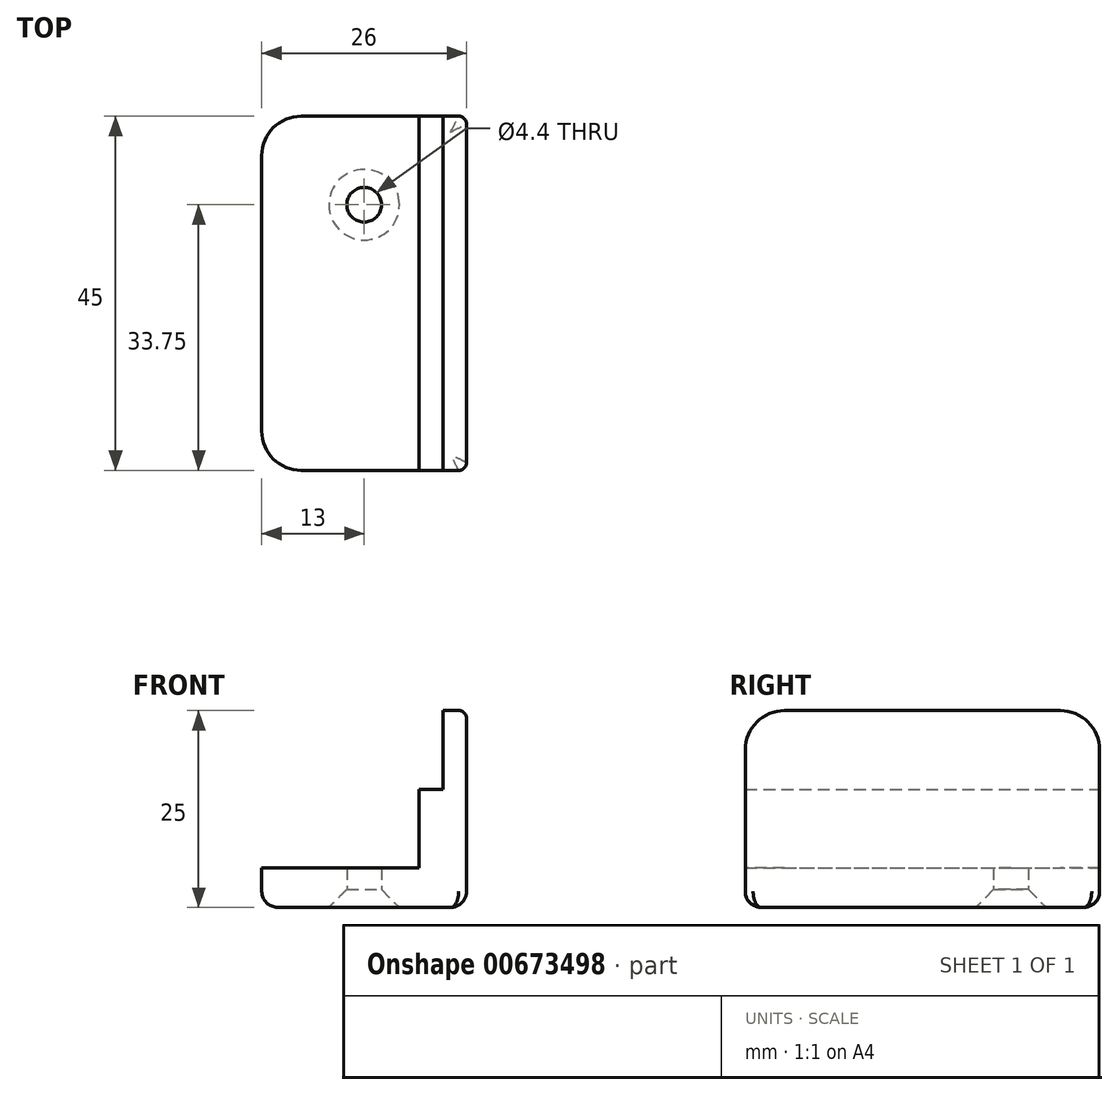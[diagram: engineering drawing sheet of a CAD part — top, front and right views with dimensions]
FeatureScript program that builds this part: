
annotation { "Feature Type Name" : "Feature", "Feature Type Description" : "" }
export const myFeature = defineFeature(function(context is Context, id is Id, definition is map)
    precondition{}
    {
        {
            var Q0;
            Q0=qCreatedBy(makeId("Front.planeOp"),FACE);
            var sketch = newSketch(context, id + "F0", { "sketchPlane" : qUnion([Q0])});
            skLineSegment(sketch, "E0", {"start": v(0, 25) * mm, "end": v(0, 0) * mm});
            skLineSegment(sketch, "E1", {"start": v(0, 0) * mm, "end": v(-26, 0) * mm});
            skLineSegment(sketch, "E2", {"start": v(-26, 0) * mm, "end": v(-26, 5) * mm});
            skLineSegment(sketch, "E3", {"start": v(-26, 5) * mm, "end": v(-6, 5) * mm});
            skLineSegment(sketch, "E4", {"start": v(-6, 5) * mm, "end": v(-6, 15) * mm});
            skLineSegment(sketch, "E5", {"start": v(-6, 15) * mm, "end": v(-3, 15) * mm});
            skLineSegment(sketch, "E6", {"start": v(-3, 15) * mm, "end": v(-3, 25) * mm});
            skLineSegment(sketch, "E7", {"start": v(-3, 25) * mm, "end": v(0, 25) * mm});
            skSolve(sketch);
        }
        {
            var Q0;
            Q0=qSketchRegion(id+"F0",true);
            extrude(context, id + "F1", {"entities" : qUnion([Q0]), "endBound" : BoundingType.SYMMETRIC, "depth" : 45 * mm, "offsetDistance" : 25 * mm});
        }
        {
            var Q0;
            Q0=makeQuery(id+"F1.opExtrude","SWEPT_FACE",FACE,{"disambiguationData":[OSD([sQuery(id+"F0.wireOp",EDGE,"E1")])]});
            var sketch = newSketch(context, id + "F2", { "sketchPlane" : qUnion([Q0])});
            skLineSegment(sketch, "E8", {"start": v(-26, 0) * mm, "end": v(0, 0) * mm, "construction": true});
            skPoint(sketch, "E9", {"position": v(-13, -11.25) * mm});
            skSolve(sketch);
        }
        {
            var Q0;
            Q0=sQuery(id+"F2.wireOp",VERTEX,"E9");
            var Q1;
            Q1=makeQuery(id+"F1.opExtrude","SWEPT_BODY",BODY,{"disambiguationData":[OSD([sQuery(id+"F0.wireOp",EDGE,"E0"),sQuery(id+"F0.wireOp",EDGE,"E1"),sQuery(id+"F0.wireOp",EDGE,"E2"),sQuery(id+"F0.wireOp",EDGE,"E3"),sQuery(id+"F0.wireOp",EDGE,"E4"),sQuery(id+"F0.wireOp",EDGE,"E5"),sQuery(id+"F0.wireOp",EDGE,"E6"),sQuery(id+"F0.wireOp",EDGE,"E7")])]});
            hole(context, id + "F3", {"style" : HoleStyle.C_SINK, "endStyle" : HoleEndStyle.THROUGH, "standardTappedOrClearance" : lookupTablePath({ "standard" : "ISO", "fit" : "Normal", "size" : "M4", "type" : "Clearance" }), "standardBlindInLast" : lookupTablePath({ "fit" : "Standard", "standard" : "ISO", "size" : "M4", "type" : "Clearance" }), "holeDiameter" : 4.4 * mm, "cSinkDiameter" : 8.96 * mm, "cSinkAngle" : 90 * degree, "majorDiameter" : 5 * mm, "isTappedThrough" : true, "tappedDepth" : 12 * mm, "tapClearance" : 3, "locations" : qUnion([Q0]), "scope" : qUnion([Q1])});
        }
        {
            var Q0;
            Q0=makeQuery(id+"F1.opExtrude","CAP_EDGE",EDGE,{"disambiguationData":[OSD([sQuery(id+"F0.wireOp",EDGE,"E2")])],"isStart":true});
            var Q1;
            Q1=makeQuery(id+"F1.opExtrude","CAP_EDGE",EDGE,{"disambiguationData":[OSD([sQuery(id+"F0.wireOp",EDGE,"E2")])],"isStart":false});
            var Q2;
            Q2=makeQuery(id+"F1.opExtrude","CAP_EDGE",EDGE,{"disambiguationData":[OSD([sQuery(id+"F0.wireOp",EDGE,"E7")])],"isStart":false});
            var Q3;
            Q3=makeQuery(id+"F1.opExtrude","CAP_EDGE",EDGE,{"disambiguationData":[OSD([sQuery(id+"F0.wireOp",EDGE,"E7")])],"isStart":true});
            fillet(context, id + "F4", {"entities" : qUnion([Q0, Q1, Q2, Q3]), "radius" : 5 * mm, "tangentPropagation" : true, "allowEdgeOverflow" : false});
        }
        {
            var Q0;
            Q0=makeQuery(id+"F1.opExtrude","CAP_EDGE",EDGE,{"disambiguationData":[OSD([sQuery(id+"F0.wireOp",EDGE,"E0")])],"isStart":true});
            fillet(context, id + "F5", {"entities" : qUnion([Q0]), "radius" : 1 * mm, "tangentPropagation" : true, "allowEdgeOverflow" : false});
        }
        {
            var Q0;
            Q0=makeQuery(id+"F1.opExtrude","SWEPT_EDGE",EDGE,{"disambiguationData":[OSD([sQuery(id+"F0.wireOp",EDGE,"E1"),sQuery(id+"F0.wireOp",EDGE,"E2")])]});
            fillet(context, id + "F6", {"entities" : qUnion([Q0]), "radius" : 2 * mm, "tangentPropagation" : true, "allowEdgeOverflow" : false});
        }
    });
